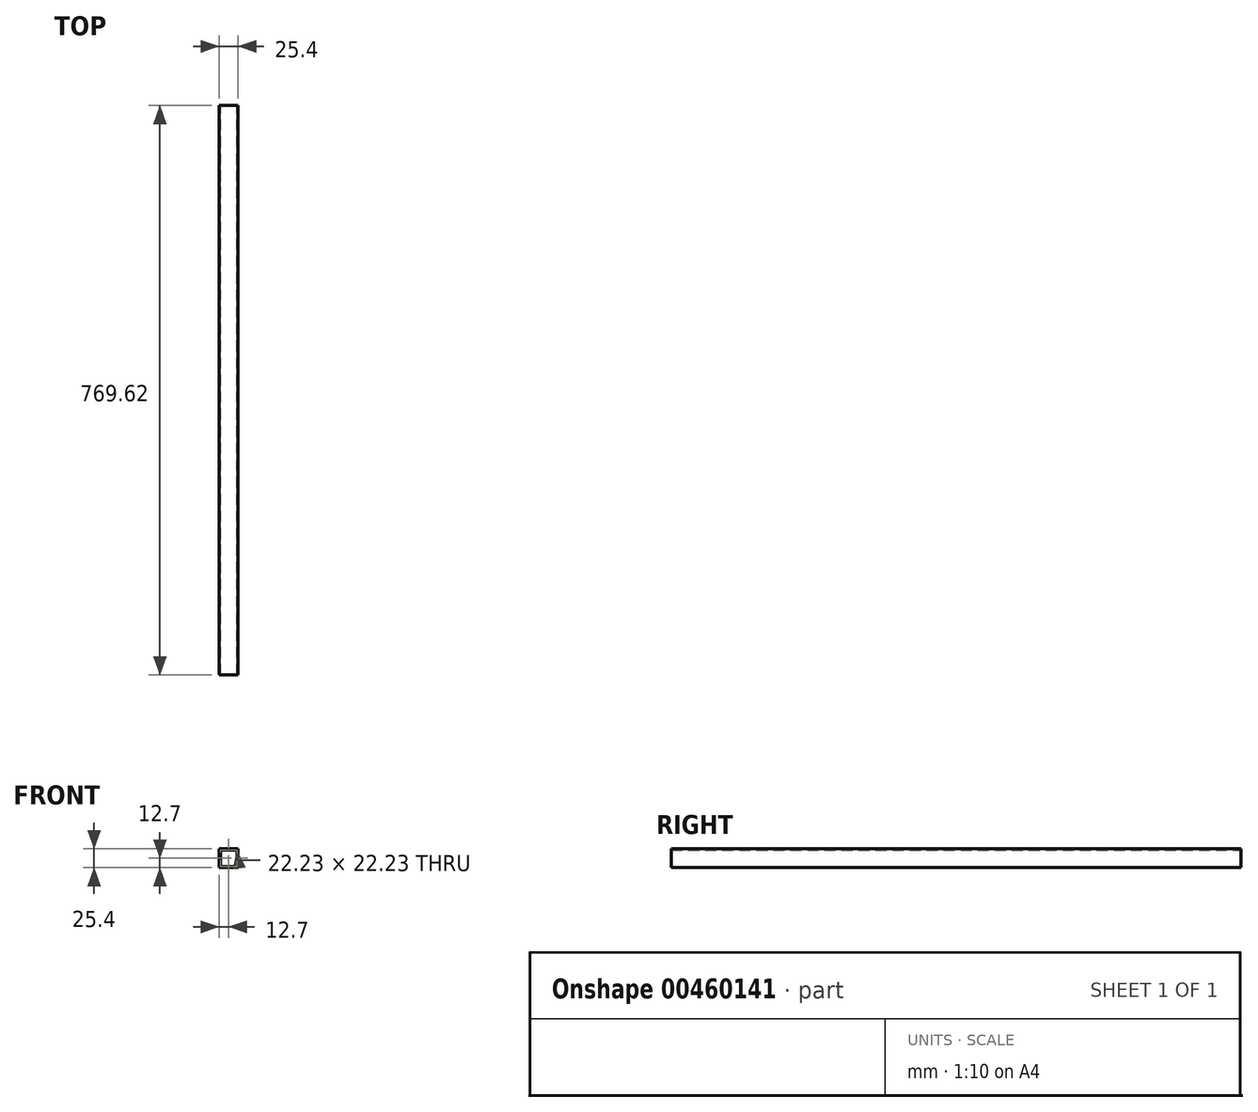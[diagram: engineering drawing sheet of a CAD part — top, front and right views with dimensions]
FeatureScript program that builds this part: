
annotation { "Feature Type Name" : "Feature", "Feature Type Description" : "" }
export const myFeature = defineFeature(function(context is Context, id is Id, definition is map)
    precondition{}
    {
        {
            var Q0;
            Q0=qCreatedBy(makeId("Front.planeOp"),FACE);
            var sketch = newSketch(context, id + "F0", { "sketchPlane" : qUnion([Q0])});
            skLineSegment(sketch, "E0.bottom", {"start": v(12.7, 12.7) * mm, "end": v(-12.7, 12.7) * mm});
            skLineSegment(sketch, "E0.top", {"start": v(12.7, -12.7) * mm, "end": v(-12.7, -12.7) * mm});
            skLineSegment(sketch, "E0.left", {"start": v(12.7, 12.7) * mm, "end": v(12.7, -12.7) * mm});
            skLineSegment(sketch, "E0.right", {"start": v(-12.7, 12.7) * mm, "end": v(-12.7, -12.7) * mm});
            skPoint(sketch, "E0.middle", {"position": v(0, 0) * mm});
            skLineSegment(sketch, "E1.bottom", {"start": v(11.11, 11.11) * mm, "end": v(-11.11, 11.11) * mm});
            skLineSegment(sketch, "E1.top", {"start": v(11.11, -11.11) * mm, "end": v(-11.11, -11.11) * mm});
            skLineSegment(sketch, "E1.left", {"start": v(11.11, 11.11) * mm, "end": v(11.11, -11.11) * mm});
            skLineSegment(sketch, "E1.right", {"start": v(-11.11, 11.11) * mm, "end": v(-11.11, -11.11) * mm});
            skSolve(sketch);
        }
        {
            var Q0;
            Q0=makeQuery(id+"F0.imprint","IMPRINT",FACE,{"disambiguationData":[TD([[makeQuery(id+"F0.imprint","IMPRINT",EDGE,{"derivedFrom":sQuery(id+"F0.wireOp",EDGE,"E0.bottom")}),1.0]])]});
            extrude(context, id + "F1", {"entities" : qUnion([Q0]), "depth" : 769.62 * mm});
        }
    });
